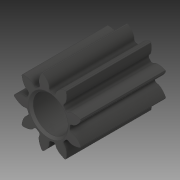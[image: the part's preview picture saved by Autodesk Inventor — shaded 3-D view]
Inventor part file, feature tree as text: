
AUTODESK INVENTOR PART (.ipt)
format: ipt  version: 2019 (Build 230136000, 136)  size: 202,240 bytes
history: native  units: in
note: dims shown in document units (in); Inventor stores cm internally (conversion verified against a paired STEP export)
features: chamfer x1
ambient origin geometry x8: Origin, YZ Plane, XZ Plane, XY Plane, X Axis, Y Axis, Z Axis, Center Point
bodies: Solid1 (feature_tree)
feature tree (1):
  chamfer  "Chamfer1"  [1 undecoded]
note: 1 required parameter value undecoded (feature->parameter linkage not recoverable at this tier; creation-order binding heuristic only, values carry confidence <= 0.55)
